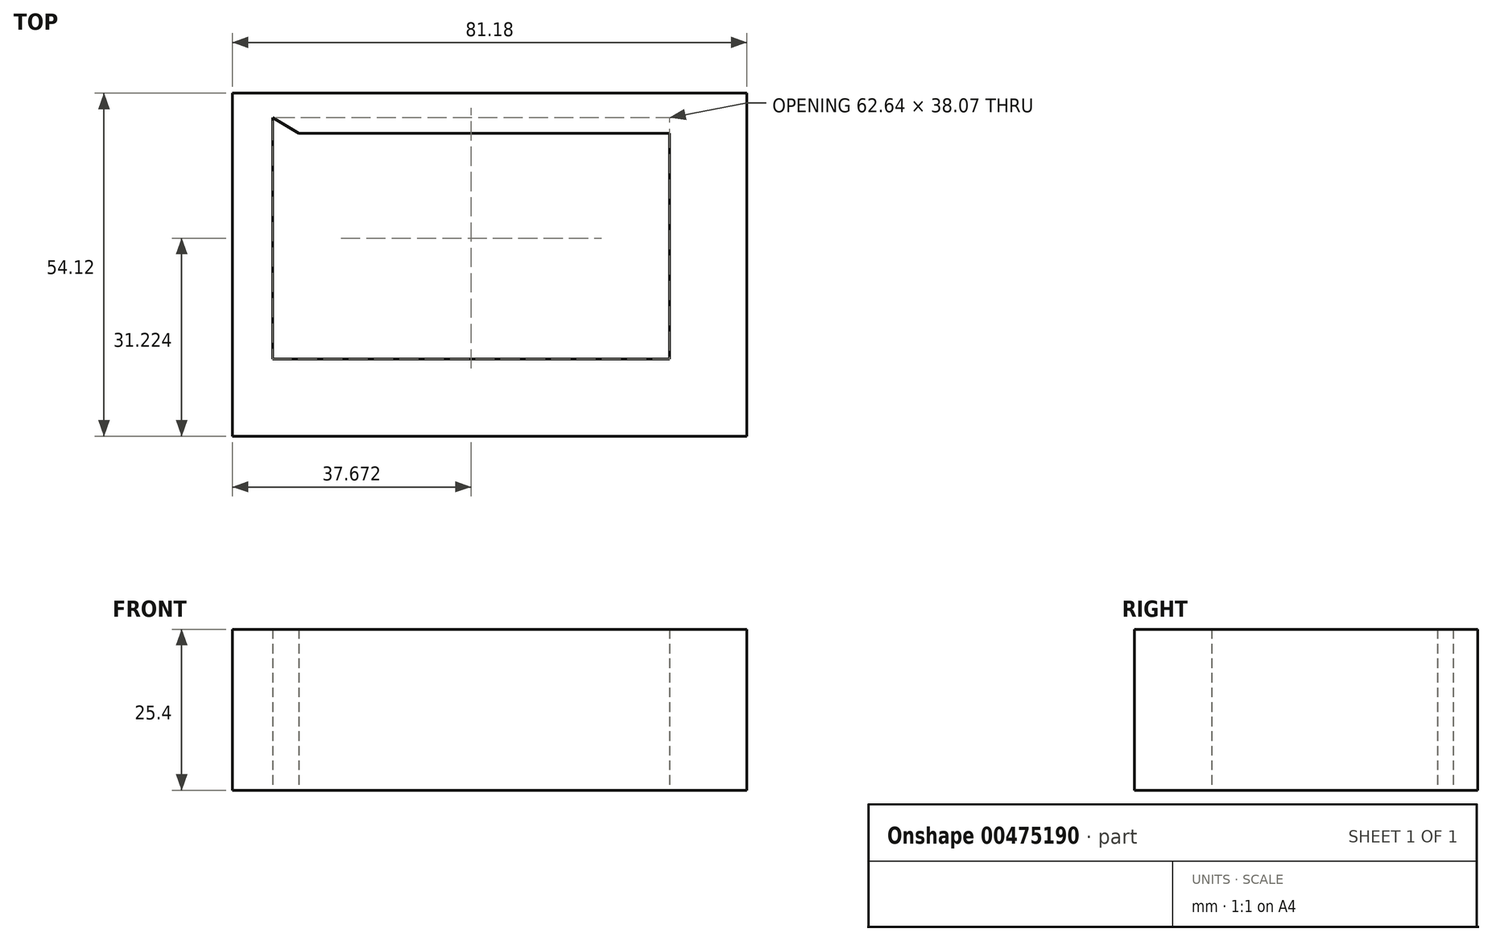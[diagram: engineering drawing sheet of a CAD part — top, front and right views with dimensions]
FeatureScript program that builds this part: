
annotation { "Feature Type Name" : "Feature", "Feature Type Description" : "" }
export const myFeature = defineFeature(function(context is Context, id is Id, definition is map)
    precondition{}
    {
        {
            var Q0;
            Q0=qCreatedBy(makeId("Top.planeOp"),FACE);
            var sketch = newSketch(context, id + "F0", { "sketchPlane" : qUnion([Q0])});
            skLineSegment(sketch, "E0.bottom", {"start": v(-36.95, -29.8) * mm, "end": v(44.23, -29.8) * mm});
            skLineSegment(sketch, "E0.top", {"start": v(-36.95, 24.33) * mm, "end": v(44.23, 24.33) * mm});
            skLineSegment(sketch, "E0.left", {"start": v(-36.95, -29.8) * mm, "end": v(-36.95, 24.33) * mm});
            skLineSegment(sketch, "E0.right", {"start": v(44.23, -29.8) * mm, "end": v(44.23, 24.33) * mm});
            skLineSegment(sketch, "E1.0", {"start": v(-36.95, 17.98) * mm, "end": v(44.23, 17.98) * mm});
            skLineSegment(sketch, "E2.0", {"start": v(-30.6, -29.8) * mm, "end": v(-30.6, 24.33) * mm});
            skLineSegment(sketch, "E3.0", {"start": v(32.04, -17.6) * mm, "end": v(32.04, 24.33) * mm});
            skLineSegment(sketch, "E3.1", {"start": v(-36.95, -17.6) * mm, "end": v(32.04, -17.6) * mm});
            skLineSegment(sketch, "E4", {"start": v(-36.95, 24.33) * mm, "end": v(32.04, -17.6) * mm});
            skSolve(sketch);
        }
        {
            var Q0;
            Q0 = qSketchRegion(id + "F0", true);
            extrude(context, id + "F1", {"entities" : qUnion([Q0]), "depth" : 25.4 * mm});
        }
    });
